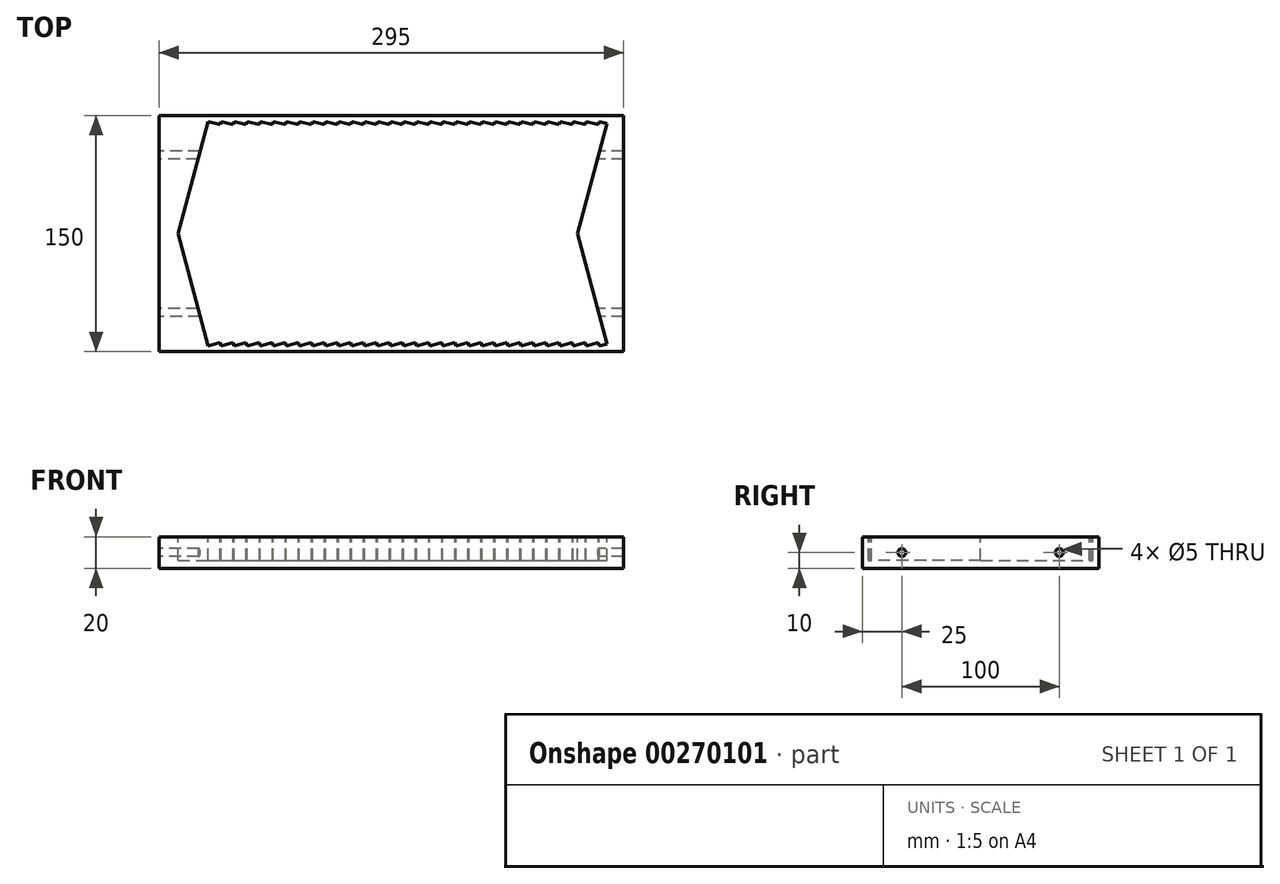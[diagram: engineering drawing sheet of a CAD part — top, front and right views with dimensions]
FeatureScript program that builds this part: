
annotation { "Feature Type Name" : "Feature", "Feature Type Description" : "" }
export const myFeature = defineFeature(function(context is Context, id is Id, definition is map)
    precondition{}
    {
        {
            var Q0;
            Q0=qCreatedBy(makeId("Top.planeOp"),FACE);
            var sketch = newSketch(context, id + "F0", { "sketchPlane" : qUnion([Q0])});
            skLineSegment(sketch, "E0.bottom", {"start": v(147.5, -75) * mm, "end": v(-147.5, -75) * mm});
            skLineSegment(sketch, "E0.top", {"start": v(147.5, 75) * mm, "end": v(-147.5, 75) * mm});
            skLineSegment(sketch, "E0.left", {"start": v(147.5, -75) * mm, "end": v(147.5, 75) * mm});
            skLineSegment(sketch, "E0.right", {"start": v(-147.5, -75) * mm, "end": v(-147.5, 75) * mm});
            skPoint(sketch, "E0.middle", {"position": v(0, 0) * mm});
            skPoint(sketch, "E1", {"position": v(0, 75) * mm});
            skPoint(sketch, "E2", {"position": v(-147.5, 0) * mm});
            skSolve(sketch);
        }
        {
            var Q0;
            Q0=makeQuery(id+"F0.imprint","IMPRINT",FACE,{"disambiguationData":[TD([[makeQuery(id+"F0.imprint","IMPRINT",EDGE,{"derivedFrom":sQuery(id+"F0.wireOp",EDGE,"E0.bottom")}),-1.0]])]});
            extrude(context, id + "F1", {"entities" : qUnion([Q0]), "depth" : 20 * mm});
        }
        {
            var Q0;
            Q0=makeQuery(id+"F1.opExtrude","SWEPT_FACE",FACE,{"disambiguationData":[OSD([sQuery(id+"F0.wireOp",EDGE,"E0.left")])]});
            var sketch = newSketch(context, id + "F2", { "sketchPlane" : qUnion([Q0])});
            skPoint(sketch, "E3", {"position": v(-50, 10) * mm});
            skPoint(sketch, "E4", {"position": v(50, 10) * mm});
            skSolve(sketch);
        }
        {
            var Q0;
            Q0=sQuery(id+"F2.wireOp",VERTEX,"E3");
            var Q1;
            Q1=sQuery(id+"F2.wireOp",VERTEX,"E4");
            var Q2;
            Q2=makeQuery(id+"F1.opExtrude","SWEPT_BODY",BODY,{"disambiguationData":[OSD([sQuery(id+"F0.wireOp",EDGE,"E0.bottom"),sQuery(id+"F0.wireOp",EDGE,"E0.top"),sQuery(id+"F0.wireOp",EDGE,"E0.left"),sQuery(id+"F0.wireOp",EDGE,"E0.right")])]});
            hole(context, id + "F3", {"style" : HoleStyle.SIMPLE, "endStyle" : HoleEndStyle.THROUGH, "standardTappedOrClearance" : lookupTablePath({ "standard" : "ISO", "engagement" : "75%", "pitch" : "1 mm", "size" : "M6", "type" : "Tapped" }), "standardBlindInLast" : lookupTablePath({ "standard" : "ISO", "engagement" : "75%", "pitch" : "1 mm", "size" : "M6", "type" : "Tapped" }), "holeDiameter" : 5 * mm, "showTappedDepth" : true, "tappedDepth" : 40 * mm, "tapClearance" : 3, "startFromSketch" : true, "locations" : qUnion([Q0, Q1]), "scope" : qUnion([Q2]), "majorDiameter" : 6 * mm});
        }
        {
            var Q0;
            Q0=makeQuery(id+"F1.opExtrude","SWEPT_FACE",FACE,{"disambiguationData":[OSD([sQuery(id+"F0.wireOp",EDGE,"E0.right")])]});
            var sketch = newSketch(context, id + "F4", { "sketchPlane" : qUnion([Q0])});
            skPoint(sketch, "E5", {"position": v(0, 10) * mm});
            skLineSegment(sketch, "E6", {"start": v(-50, 10) * mm, "end": v(50, 10) * mm, "construction": true});
            skSolve(sketch);
        }
        {
            var Q0;
            Q0=makeQuery(id+"F1.opExtrude","CAP_FACE",FACE,{"disambiguationData":[OSD([sQuery(id+"F0.wireOp",EDGE,"E0.bottom"),sQuery(id+"F0.wireOp",EDGE,"E0.top"),sQuery(id+"F0.wireOp",EDGE,"E0.left"),sQuery(id+"F0.wireOp",EDGE,"E0.right")])],"isStart":false});
            var sketch = newSketch(context, id + "F5", { "sketchPlane" : qUnion([Q0])});
            skLineSegment(sketch, "E7", {"start": v(-135.5, 0) * mm, "end": v(-116.4, 71.3) * mm});
            skLineSegment(sketch, "E8", {"start": v(-135.5, 0) * mm, "end": v(-116.4, -71.3) * mm});
            skLineSegment(sketch, "E9.0", {"start": v(-130.32, 0) * mm, "end": v(-111.57, 70) * mm});
            skLineSegment(sketch, "E9.1", {"start": v(-130.32, 0) * mm, "end": v(-111.57, -70) * mm});
            skLineSegment(sketch, "E10", {"start": v(-116.4, 71.3) * mm, "end": v(-111.57, 70) * mm});
            skLineSegment(sketch, "E11", {"start": v(-116.4, -71.3) * mm, "end": v(-111.57, -70) * mm});
            skLineSegment(sketch, "E12.0", {"start": v(-127.22, 0) * mm, "end": v(-108.67, 69.22) * mm});
            skLineSegment(sketch, "E12.1", {"start": v(-127.22, 0) * mm, "end": v(-108.67, -69.22) * mm});
            skLineSegment(sketch, "E13", {"start": v(-111.57, 70) * mm, "end": v(-108.67, 69.22) * mm});
            skLineSegment(sketch, "E14", {"start": v(-111.57, -70) * mm, "end": v(-108.67, -69.22) * mm});
            skLineSegment(sketch, "E15.1.0.0", {"start": v(-118.94, 0) * mm, "end": v(-100.39, 69.22) * mm});
            skLineSegment(sketch, "E15.1.0.1", {"start": v(-122.04, 0) * mm, "end": v(-103.28, 70) * mm});
            skLineSegment(sketch, "E15.1.0.2", {"start": v(-127.22, 0) * mm, "end": v(-108.11, 71.3) * mm});
            skLineSegment(sketch, "E15.1.0.3", {"start": v(-127.22, 0) * mm, "end": v(-108.11, -71.3) * mm});
            skLineSegment(sketch, "E15.1.0.4", {"start": v(-122.04, 0) * mm, "end": v(-103.28, -70) * mm});
            skLineSegment(sketch, "E15.1.0.5", {"start": v(-118.94, 0) * mm, "end": v(-100.39, -69.22) * mm});
            skLineSegment(sketch, "E15.1.0.6", {"start": v(-108.11, -71.3) * mm, "end": v(-103.28, -70) * mm});
            skLineSegment(sketch, "E15.1.0.7", {"start": v(-103.28, -70) * mm, "end": v(-100.39, -69.22) * mm});
            skLineSegment(sketch, "E15.1.0.8", {"start": v(-108.11, 71.3) * mm, "end": v(-103.28, 70) * mm});
            skLineSegment(sketch, "E15.1.0.9", {"start": v(-103.28, 70) * mm, "end": v(-100.39, 69.22) * mm});
            skLineSegment(sketch, "E15.2.0.0", {"start": v(-110.65, 0) * mm, "end": v(-92.1, 69.22) * mm});
            skLineSegment(sketch, "E15.2.0.1", {"start": v(-113.76, 0) * mm, "end": v(-95, 70) * mm});
            skLineSegment(sketch, "E15.2.0.2", {"start": v(-118.94, 0) * mm, "end": v(-99.83, 71.3) * mm});
            skLineSegment(sketch, "E15.2.0.3", {"start": v(-118.94, 0) * mm, "end": v(-99.83, -71.3) * mm});
            skLineSegment(sketch, "E15.2.0.4", {"start": v(-113.76, 0) * mm, "end": v(-95, -70) * mm});
            skLineSegment(sketch, "E15.2.0.5", {"start": v(-110.65, 0) * mm, "end": v(-92.1, -69.22) * mm});
            skLineSegment(sketch, "E15.2.0.6", {"start": v(-99.83, -71.3) * mm, "end": v(-95, -70) * mm});
            skLineSegment(sketch, "E15.2.0.7", {"start": v(-95, -70) * mm, "end": v(-92.1, -69.22) * mm});
            skLineSegment(sketch, "E15.2.0.8", {"start": v(-99.83, 71.3) * mm, "end": v(-95, 70) * mm});
            skLineSegment(sketch, "E15.2.0.9", {"start": v(-95, 70) * mm, "end": v(-92.1, 69.22) * mm});
            skLineSegment(sketch, "E15.direction1", {"start": v(-127.22, 0) * mm, "end": v(-118.94, 0) * mm, "construction": true});
            skLineSegment(sketch, "E16.0.3.0", {"start": v(-102.37, 0) * mm, "end": v(-83.82, 69.22) * mm});
            skLineSegment(sketch, "E16.3.3.0", {"start": v(-105.48, 0) * mm, "end": v(-86.72, 70) * mm});
            skLineSegment(sketch, "E16.6.3.0", {"start": v(-110.65, 0) * mm, "end": v(-91.55, 71.3) * mm});
            skLineSegment(sketch, "E16.9.3.0", {"start": v(-110.65, 0) * mm, "end": v(-91.55, -71.3) * mm});
            skLineSegment(sketch, "E16.12.3.0", {"start": v(-105.48, 0) * mm, "end": v(-86.72, -70) * mm});
            skLineSegment(sketch, "E16.15.3.0", {"start": v(-102.37, 0) * mm, "end": v(-83.82, -69.22) * mm});
            skLineSegment(sketch, "E16.18.3.0", {"start": v(-91.55, -71.3) * mm, "end": v(-86.72, -70) * mm});
            skLineSegment(sketch, "E16.21.3.0", {"start": v(-86.72, -70) * mm, "end": v(-83.82, -69.22) * mm});
            skLineSegment(sketch, "E16.24.3.0", {"start": v(-91.55, 71.3) * mm, "end": v(-86.72, 70) * mm});
            skLineSegment(sketch, "E16.27.3.0", {"start": v(-86.72, 70) * mm, "end": v(-83.82, 69.22) * mm});
            skLineSegment(sketch, "E16.0.4.0", {"start": v(-94.09, 0) * mm, "end": v(-75.54, 69.22) * mm});
            skLineSegment(sketch, "E16.3.4.0", {"start": v(-97.2, 0) * mm, "end": v(-78.44, 70) * mm});
            skLineSegment(sketch, "E16.6.4.0", {"start": v(-102.37, 0) * mm, "end": v(-83.27, 71.3) * mm});
            skLineSegment(sketch, "E16.9.4.0", {"start": v(-102.37, 0) * mm, "end": v(-83.27, -71.3) * mm});
            skLineSegment(sketch, "E16.12.4.0", {"start": v(-97.2, 0) * mm, "end": v(-78.44, -70) * mm});
            skLineSegment(sketch, "E16.15.4.0", {"start": v(-94.09, 0) * mm, "end": v(-75.54, -69.22) * mm});
            skLineSegment(sketch, "E16.18.4.0", {"start": v(-83.27, -71.3) * mm, "end": v(-78.44, -70) * mm});
            skLineSegment(sketch, "E16.21.4.0", {"start": v(-78.44, -70) * mm, "end": v(-75.54, -69.22) * mm});
            skLineSegment(sketch, "E16.24.4.0", {"start": v(-83.27, 71.3) * mm, "end": v(-78.44, 70) * mm});
            skLineSegment(sketch, "E16.27.4.0", {"start": v(-78.44, 70) * mm, "end": v(-75.54, 69.22) * mm});
            skLineSegment(sketch, "E16.0.5.0", {"start": v(-85.8, 0) * mm, "end": v(-67.26, 69.22) * mm});
            skLineSegment(sketch, "E16.3.5.0", {"start": v(-88.91, 0) * mm, "end": v(-70.16, 70) * mm});
            skLineSegment(sketch, "E16.6.5.0", {"start": v(-94.09, 0) * mm, "end": v(-74.99, 71.3) * mm});
            skLineSegment(sketch, "E16.9.5.0", {"start": v(-94.09, 0) * mm, "end": v(-74.99, -71.3) * mm});
            skLineSegment(sketch, "E16.12.5.0", {"start": v(-88.91, 0) * mm, "end": v(-70.16, -70) * mm});
            skLineSegment(sketch, "E16.15.5.0", {"start": v(-85.8, 0) * mm, "end": v(-67.26, -69.22) * mm});
            skLineSegment(sketch, "E16.18.5.0", {"start": v(-74.99, -71.3) * mm, "end": v(-70.16, -70) * mm});
            skLineSegment(sketch, "E16.21.5.0", {"start": v(-70.16, -70) * mm, "end": v(-67.26, -69.22) * mm});
            skLineSegment(sketch, "E16.24.5.0", {"start": v(-74.99, 71.3) * mm, "end": v(-70.16, 70) * mm});
            skLineSegment(sketch, "E16.27.5.0", {"start": v(-70.16, 70) * mm, "end": v(-67.26, 69.22) * mm});
            skLineSegment(sketch, "E16.0.6.0", {"start": v(-77.52, 0) * mm, "end": v(-58.98, 69.22) * mm});
            skLineSegment(sketch, "E16.3.6.0", {"start": v(-80.63, 0) * mm, "end": v(-61.87, 70) * mm});
            skLineSegment(sketch, "E16.6.6.0", {"start": v(-85.8, 0) * mm, "end": v(-66.7, 71.3) * mm});
            skLineSegment(sketch, "E16.9.6.0", {"start": v(-85.8, 0) * mm, "end": v(-66.7, -71.3) * mm});
            skLineSegment(sketch, "E16.12.6.0", {"start": v(-80.63, 0) * mm, "end": v(-61.87, -70) * mm});
            skLineSegment(sketch, "E16.15.6.0", {"start": v(-77.52, 0) * mm, "end": v(-58.98, -69.22) * mm});
            skLineSegment(sketch, "E16.18.6.0", {"start": v(-66.7, -71.3) * mm, "end": v(-61.87, -70) * mm});
            skLineSegment(sketch, "E16.21.6.0", {"start": v(-61.87, -70) * mm, "end": v(-58.98, -69.22) * mm});
            skLineSegment(sketch, "E16.24.6.0", {"start": v(-66.7, 71.3) * mm, "end": v(-61.87, 70) * mm});
            skLineSegment(sketch, "E16.27.6.0", {"start": v(-61.87, 70) * mm, "end": v(-58.98, 69.22) * mm});
            skLineSegment(sketch, "E16.0.7.0", {"start": v(-69.24, 0) * mm, "end": v(-50.7, 69.22) * mm});
            skLineSegment(sketch, "E16.3.7.0", {"start": v(-72.35, 0) * mm, "end": v(-53.6, 70) * mm});
            skLineSegment(sketch, "E16.6.7.0", {"start": v(-77.52, 0) * mm, "end": v(-58.42, 71.3) * mm});
            skLineSegment(sketch, "E16.9.7.0", {"start": v(-77.52, 0) * mm, "end": v(-58.42, -71.3) * mm});
            skLineSegment(sketch, "E16.12.7.0", {"start": v(-72.35, 0) * mm, "end": v(-53.6, -70) * mm});
            skLineSegment(sketch, "E16.15.7.0", {"start": v(-69.24, 0) * mm, "end": v(-50.7, -69.22) * mm});
            skLineSegment(sketch, "E16.18.7.0", {"start": v(-58.42, -71.3) * mm, "end": v(-53.6, -70) * mm});
            skLineSegment(sketch, "E16.21.7.0", {"start": v(-53.6, -70) * mm, "end": v(-50.7, -69.22) * mm});
            skLineSegment(sketch, "E16.24.7.0", {"start": v(-58.42, 71.3) * mm, "end": v(-53.6, 70) * mm});
            skLineSegment(sketch, "E16.27.7.0", {"start": v(-53.6, 70) * mm, "end": v(-50.7, 69.22) * mm});
            skLineSegment(sketch, "E16.0.8.0", {"start": v(-60.96, 0) * mm, "end": v(-42.41, 69.22) * mm});
            skLineSegment(sketch, "E16.3.8.0", {"start": v(-64.07, 0) * mm, "end": v(-45.3, 70) * mm});
            skLineSegment(sketch, "E16.6.8.0", {"start": v(-69.24, 0) * mm, "end": v(-50.14, 71.3) * mm});
            skLineSegment(sketch, "E16.9.8.0", {"start": v(-69.24, 0) * mm, "end": v(-50.14, -71.3) * mm});
            skLineSegment(sketch, "E16.12.8.0", {"start": v(-64.07, 0) * mm, "end": v(-45.3, -70) * mm});
            skLineSegment(sketch, "E16.15.8.0", {"start": v(-60.96, 0) * mm, "end": v(-42.41, -69.22) * mm});
            skLineSegment(sketch, "E16.18.8.0", {"start": v(-50.14, -71.3) * mm, "end": v(-45.3, -70) * mm});
            skLineSegment(sketch, "E16.21.8.0", {"start": v(-45.3, -70) * mm, "end": v(-42.41, -69.22) * mm});
            skLineSegment(sketch, "E16.24.8.0", {"start": v(-50.14, 71.3) * mm, "end": v(-45.3, 70) * mm});
            skLineSegment(sketch, "E16.27.8.0", {"start": v(-45.3, 70) * mm, "end": v(-42.41, 69.22) * mm});
            skLineSegment(sketch, "E16.0.9.0", {"start": v(-52.68, 0) * mm, "end": v(-34.13, 69.22) * mm});
            skLineSegment(sketch, "E16.3.9.0", {"start": v(-55.78, 0) * mm, "end": v(-37.03, 70) * mm});
            skLineSegment(sketch, "E16.6.9.0", {"start": v(-60.96, 0) * mm, "end": v(-41.86, 71.3) * mm});
            skLineSegment(sketch, "E16.9.9.0", {"start": v(-60.96, 0) * mm, "end": v(-41.86, -71.3) * mm});
            skLineSegment(sketch, "E16.12.9.0", {"start": v(-55.78, 0) * mm, "end": v(-37.03, -70) * mm});
            skLineSegment(sketch, "E16.15.9.0", {"start": v(-52.68, 0) * mm, "end": v(-34.13, -69.22) * mm});
            skLineSegment(sketch, "E16.18.9.0", {"start": v(-41.86, -71.3) * mm, "end": v(-37.03, -70) * mm});
            skLineSegment(sketch, "E16.21.9.0", {"start": v(-37.03, -70) * mm, "end": v(-34.13, -69.22) * mm});
            skLineSegment(sketch, "E16.24.9.0", {"start": v(-41.86, 71.3) * mm, "end": v(-37.03, 70) * mm});
            skLineSegment(sketch, "E16.27.9.0", {"start": v(-37.03, 70) * mm, "end": v(-34.13, 69.22) * mm});
            skLineSegment(sketch, "E16.0.10.0", {"start": v(-44.4, 0) * mm, "end": v(-25.85, 69.22) * mm});
            skLineSegment(sketch, "E16.3.10.0", {"start": v(-47.5, 0) * mm, "end": v(-28.75, 70) * mm});
            skLineSegment(sketch, "E16.6.10.0", {"start": v(-52.68, 0) * mm, "end": v(-33.57, 71.3) * mm});
            skLineSegment(sketch, "E16.9.10.0", {"start": v(-52.68, 0) * mm, "end": v(-33.57, -71.3) * mm});
            skLineSegment(sketch, "E16.12.10.0", {"start": v(-47.5, 0) * mm, "end": v(-28.75, -70) * mm});
            skLineSegment(sketch, "E16.15.10.0", {"start": v(-44.4, 0) * mm, "end": v(-25.85, -69.22) * mm});
            skLineSegment(sketch, "E16.18.10.0", {"start": v(-33.57, -71.3) * mm, "end": v(-28.75, -70) * mm});
            skLineSegment(sketch, "E16.21.10.0", {"start": v(-28.75, -70) * mm, "end": v(-25.85, -69.22) * mm});
            skLineSegment(sketch, "E16.24.10.0", {"start": v(-33.57, 71.3) * mm, "end": v(-28.75, 70) * mm});
            skLineSegment(sketch, "E16.27.10.0", {"start": v(-28.75, 70) * mm, "end": v(-25.85, 69.22) * mm});
            skLineSegment(sketch, "E16.0.11.0", {"start": v(-36.11, 0) * mm, "end": v(-17.57, 69.22) * mm});
            skLineSegment(sketch, "E16.3.11.0", {"start": v(-39.22, 0) * mm, "end": v(-20.46, 70) * mm});
            skLineSegment(sketch, "E16.6.11.0", {"start": v(-44.4, 0) * mm, "end": v(-25.3, 71.3) * mm});
            skLineSegment(sketch, "E16.9.11.0", {"start": v(-44.4, 0) * mm, "end": v(-25.3, -71.3) * mm});
            skLineSegment(sketch, "E16.12.11.0", {"start": v(-39.22, 0) * mm, "end": v(-20.46, -70) * mm});
            skLineSegment(sketch, "E16.15.11.0", {"start": v(-36.11, 0) * mm, "end": v(-17.57, -69.22) * mm});
            skLineSegment(sketch, "E16.18.11.0", {"start": v(-25.3, -71.3) * mm, "end": v(-20.46, -70) * mm});
            skLineSegment(sketch, "E16.21.11.0", {"start": v(-20.46, -70) * mm, "end": v(-17.57, -69.22) * mm});
            skLineSegment(sketch, "E16.24.11.0", {"start": v(-25.3, 71.3) * mm, "end": v(-20.46, 70) * mm});
            skLineSegment(sketch, "E16.27.11.0", {"start": v(-20.46, 70) * mm, "end": v(-17.57, 69.22) * mm});
            skLineSegment(sketch, "E16.0.12.0", {"start": v(-27.83, 0) * mm, "end": v(-9.28, 69.22) * mm});
            skLineSegment(sketch, "E16.3.12.0", {"start": v(-30.94, 0) * mm, "end": v(-12.18, 70) * mm});
            skLineSegment(sketch, "E16.6.12.0", {"start": v(-36.11, 0) * mm, "end": v(-17.01, 71.3) * mm});
            skLineSegment(sketch, "E16.9.12.0", {"start": v(-36.11, 0) * mm, "end": v(-17.01, -71.3) * mm});
            skLineSegment(sketch, "E16.12.12.0", {"start": v(-30.94, 0) * mm, "end": v(-12.18, -70) * mm});
            skLineSegment(sketch, "E16.15.12.0", {"start": v(-27.83, 0) * mm, "end": v(-9.28, -69.22) * mm});
            skLineSegment(sketch, "E16.18.12.0", {"start": v(-17.01, -71.3) * mm, "end": v(-12.18, -70) * mm});
            skLineSegment(sketch, "E16.21.12.0", {"start": v(-12.18, -70) * mm, "end": v(-9.28, -69.22) * mm});
            skLineSegment(sketch, "E16.24.12.0", {"start": v(-17.01, 71.3) * mm, "end": v(-12.18, 70) * mm});
            skLineSegment(sketch, "E16.27.12.0", {"start": v(-12.18, 70) * mm, "end": v(-9.28, 69.22) * mm});
            skLineSegment(sketch, "E16.0.13.0", {"start": v(-19.55, 0) * mm, "end": v(-1, 69.22) * mm});
            skLineSegment(sketch, "E16.3.13.0", {"start": v(-22.65, 0) * mm, "end": v(-3.9, 70) * mm});
            skLineSegment(sketch, "E16.6.13.0", {"start": v(-27.83, 0) * mm, "end": v(-8.73, 71.3) * mm});
            skLineSegment(sketch, "E16.9.13.0", {"start": v(-27.83, 0) * mm, "end": v(-8.73, -71.3) * mm});
            skLineSegment(sketch, "E16.12.13.0", {"start": v(-22.65, 0) * mm, "end": v(-3.9, -70) * mm});
            skLineSegment(sketch, "E16.15.13.0", {"start": v(-19.55, 0) * mm, "end": v(-1, -69.22) * mm});
            skLineSegment(sketch, "E16.18.13.0", {"start": v(-8.73, -71.3) * mm, "end": v(-3.9, -70) * mm});
            skLineSegment(sketch, "E16.21.13.0", {"start": v(-3.9, -70) * mm, "end": v(-1, -69.22) * mm});
            skLineSegment(sketch, "E16.24.13.0", {"start": v(-8.73, 71.3) * mm, "end": v(-3.9, 70) * mm});
            skLineSegment(sketch, "E16.27.13.0", {"start": v(-3.9, 70) * mm, "end": v(-1, 69.22) * mm});
            skLineSegment(sketch, "E16.0.14.0", {"start": v(-11.27, 0) * mm, "end": v(7.28, 69.22) * mm});
            skLineSegment(sketch, "E16.3.14.0", {"start": v(-14.37, 0) * mm, "end": v(4.38, 70) * mm});
            skLineSegment(sketch, "E16.6.14.0", {"start": v(-19.55, 0) * mm, "end": v(-0.45, 71.3) * mm});
            skLineSegment(sketch, "E16.9.14.0", {"start": v(-19.55, 0) * mm, "end": v(-0.45, -71.3) * mm});
            skLineSegment(sketch, "E16.12.14.0", {"start": v(-14.37, 0) * mm, "end": v(4.38, -70) * mm});
            skLineSegment(sketch, "E16.15.14.0", {"start": v(-11.27, 0) * mm, "end": v(7.28, -69.22) * mm});
            skLineSegment(sketch, "E16.18.14.0", {"start": v(-0.45, -71.3) * mm, "end": v(4.38, -70) * mm});
            skLineSegment(sketch, "E16.21.14.0", {"start": v(4.38, -70) * mm, "end": v(7.28, -69.22) * mm});
            skLineSegment(sketch, "E16.24.14.0", {"start": v(-0.45, 71.3) * mm, "end": v(4.38, 70) * mm});
            skLineSegment(sketch, "E16.27.14.0", {"start": v(4.38, 70) * mm, "end": v(7.28, 69.22) * mm});
            skLineSegment(sketch, "E16.0.15.0", {"start": v(-2.98, 0) * mm, "end": v(15.56, 69.22) * mm});
            skLineSegment(sketch, "E16.3.15.0", {"start": v(-6.1, 0) * mm, "end": v(12.67, 70) * mm});
            skLineSegment(sketch, "E16.6.15.0", {"start": v(-11.27, 0) * mm, "end": v(7.84, 71.3) * mm});
            skLineSegment(sketch, "E16.9.15.0", {"start": v(-11.27, 0) * mm, "end": v(7.84, -71.3) * mm});
            skLineSegment(sketch, "E16.12.15.0", {"start": v(-6.1, 0) * mm, "end": v(12.67, -70) * mm});
            skLineSegment(sketch, "E16.15.15.0", {"start": v(-2.98, 0) * mm, "end": v(15.56, -69.22) * mm});
            skLineSegment(sketch, "E16.18.15.0", {"start": v(7.84, -71.3) * mm, "end": v(12.67, -70) * mm});
            skLineSegment(sketch, "E16.21.15.0", {"start": v(12.67, -70) * mm, "end": v(15.56, -69.22) * mm});
            skLineSegment(sketch, "E16.24.15.0", {"start": v(7.84, 71.3) * mm, "end": v(12.67, 70) * mm});
            skLineSegment(sketch, "E16.27.15.0", {"start": v(12.67, 70) * mm, "end": v(15.56, 69.22) * mm});
            skLineSegment(sketch, "E16.0.16.0", {"start": v(5.3, 0) * mm, "end": v(23.85, 69.22) * mm});
            skLineSegment(sketch, "E16.3.16.0", {"start": v(2.2, 0) * mm, "end": v(20.95, 70) * mm});
            skLineSegment(sketch, "E16.6.16.0", {"start": v(-2.98, 0) * mm, "end": v(16.12, 71.3) * mm});
            skLineSegment(sketch, "E16.9.16.0", {"start": v(-2.98, 0) * mm, "end": v(16.12, -71.3) * mm});
            skLineSegment(sketch, "E16.12.16.0", {"start": v(2.2, 0) * mm, "end": v(20.95, -70) * mm});
            skLineSegment(sketch, "E16.15.16.0", {"start": v(5.3, 0) * mm, "end": v(23.85, -69.22) * mm});
            skLineSegment(sketch, "E16.18.16.0", {"start": v(16.12, -71.3) * mm, "end": v(20.95, -70) * mm});
            skLineSegment(sketch, "E16.21.16.0", {"start": v(20.95, -70) * mm, "end": v(23.85, -69.22) * mm});
            skLineSegment(sketch, "E16.24.16.0", {"start": v(16.12, 71.3) * mm, "end": v(20.95, 70) * mm});
            skLineSegment(sketch, "E16.27.16.0", {"start": v(20.95, 70) * mm, "end": v(23.85, 69.22) * mm});
            skLineSegment(sketch, "E16.0.17.0", {"start": v(13.58, 0) * mm, "end": v(32.13, 69.22) * mm});
            skLineSegment(sketch, "E16.3.17.0", {"start": v(10.47, 0) * mm, "end": v(29.23, 70) * mm});
            skLineSegment(sketch, "E16.6.17.0", {"start": v(5.3, 0) * mm, "end": v(24.4, 71.3) * mm});
            skLineSegment(sketch, "E16.9.17.0", {"start": v(5.3, 0) * mm, "end": v(24.4, -71.3) * mm});
            skLineSegment(sketch, "E16.12.17.0", {"start": v(10.47, 0) * mm, "end": v(29.23, -70) * mm});
            skLineSegment(sketch, "E16.15.17.0", {"start": v(13.58, 0) * mm, "end": v(32.13, -69.22) * mm});
            skLineSegment(sketch, "E16.18.17.0", {"start": v(24.4, -71.3) * mm, "end": v(29.23, -70) * mm});
            skLineSegment(sketch, "E16.21.17.0", {"start": v(29.23, -70) * mm, "end": v(32.13, -69.22) * mm});
            skLineSegment(sketch, "E16.24.17.0", {"start": v(24.4, 71.3) * mm, "end": v(29.23, 70) * mm});
            skLineSegment(sketch, "E16.27.17.0", {"start": v(29.23, 70) * mm, "end": v(32.13, 69.22) * mm});
            skLineSegment(sketch, "E16.0.18.0", {"start": v(21.86, 0) * mm, "end": v(40.41, 69.22) * mm});
            skLineSegment(sketch, "E16.3.18.0", {"start": v(18.76, 0) * mm, "end": v(37.51, 70) * mm});
            skLineSegment(sketch, "E16.6.18.0", {"start": v(13.58, 0) * mm, "end": v(32.68, 71.3) * mm});
            skLineSegment(sketch, "E16.9.18.0", {"start": v(13.58, 0) * mm, "end": v(32.68, -71.3) * mm});
            skLineSegment(sketch, "E16.12.18.0", {"start": v(18.76, 0) * mm, "end": v(37.51, -70) * mm});
            skLineSegment(sketch, "E16.15.18.0", {"start": v(21.86, 0) * mm, "end": v(40.41, -69.22) * mm});
            skLineSegment(sketch, "E16.18.18.0", {"start": v(32.68, -71.3) * mm, "end": v(37.51, -70) * mm});
            skLineSegment(sketch, "E16.21.18.0", {"start": v(37.51, -70) * mm, "end": v(40.41, -69.22) * mm});
            skLineSegment(sketch, "E16.24.18.0", {"start": v(32.68, 71.3) * mm, "end": v(37.51, 70) * mm});
            skLineSegment(sketch, "E16.27.18.0", {"start": v(37.51, 70) * mm, "end": v(40.41, 69.22) * mm});
            skLineSegment(sketch, "E16.0.19.0", {"start": v(30.14, 0) * mm, "end": v(48.7, 69.22) * mm});
            skLineSegment(sketch, "E16.3.19.0", {"start": v(27.04, 0) * mm, "end": v(45.8, 70) * mm});
            skLineSegment(sketch, "E16.6.19.0", {"start": v(21.86, 0) * mm, "end": v(40.97, 71.3) * mm});
            skLineSegment(sketch, "E16.9.19.0", {"start": v(21.86, 0) * mm, "end": v(40.97, -71.3) * mm});
            skLineSegment(sketch, "E16.12.19.0", {"start": v(27.04, 0) * mm, "end": v(45.8, -70) * mm});
            skLineSegment(sketch, "E16.15.19.0", {"start": v(30.14, 0) * mm, "end": v(48.7, -69.22) * mm});
            skLineSegment(sketch, "E16.18.19.0", {"start": v(40.97, -71.3) * mm, "end": v(45.8, -70) * mm});
            skLineSegment(sketch, "E16.21.19.0", {"start": v(45.8, -70) * mm, "end": v(48.7, -69.22) * mm});
            skLineSegment(sketch, "E16.24.19.0", {"start": v(40.97, 71.3) * mm, "end": v(45.8, 70) * mm});
            skLineSegment(sketch, "E16.27.19.0", {"start": v(45.8, 70) * mm, "end": v(48.7, 69.22) * mm});
            skLineSegment(sketch, "E16.0.20.0", {"start": v(38.43, 0) * mm, "end": v(56.97, 69.22) * mm});
            skLineSegment(sketch, "E16.3.20.0", {"start": v(35.32, 0) * mm, "end": v(54.08, 70) * mm});
            skLineSegment(sketch, "E16.6.20.0", {"start": v(30.14, 0) * mm, "end": v(49.25, 71.3) * mm});
            skLineSegment(sketch, "E16.9.20.0", {"start": v(30.14, 0) * mm, "end": v(49.25, -71.3) * mm});
            skLineSegment(sketch, "E16.12.20.0", {"start": v(35.32, 0) * mm, "end": v(54.08, -70) * mm});
            skLineSegment(sketch, "E16.15.20.0", {"start": v(38.43, 0) * mm, "end": v(56.97, -69.22) * mm});
            skLineSegment(sketch, "E16.18.20.0", {"start": v(49.25, -71.3) * mm, "end": v(54.08, -70) * mm});
            skLineSegment(sketch, "E16.21.20.0", {"start": v(54.08, -70) * mm, "end": v(56.97, -69.22) * mm});
            skLineSegment(sketch, "E16.24.20.0", {"start": v(49.25, 71.3) * mm, "end": v(54.08, 70) * mm});
            skLineSegment(sketch, "E16.27.20.0", {"start": v(54.08, 70) * mm, "end": v(56.97, 69.22) * mm});
            skLineSegment(sketch, "E16.0.21.0", {"start": v(46.7, 0) * mm, "end": v(65.26, 69.22) * mm});
            skLineSegment(sketch, "E16.3.21.0", {"start": v(43.6, 0) * mm, "end": v(62.36, 70) * mm});
            skLineSegment(sketch, "E16.6.21.0", {"start": v(38.43, 0) * mm, "end": v(57.53, 71.3) * mm});
            skLineSegment(sketch, "E16.9.21.0", {"start": v(38.43, 0) * mm, "end": v(57.53, -71.3) * mm});
            skLineSegment(sketch, "E16.12.21.0", {"start": v(43.6, 0) * mm, "end": v(62.36, -70) * mm});
            skLineSegment(sketch, "E16.15.21.0", {"start": v(46.7, 0) * mm, "end": v(65.26, -69.22) * mm});
            skLineSegment(sketch, "E16.18.21.0", {"start": v(57.53, -71.3) * mm, "end": v(62.36, -70) * mm});
            skLineSegment(sketch, "E16.21.21.0", {"start": v(62.36, -70) * mm, "end": v(65.26, -69.22) * mm});
            skLineSegment(sketch, "E16.24.21.0", {"start": v(57.53, 71.3) * mm, "end": v(62.36, 70) * mm});
            skLineSegment(sketch, "E16.27.21.0", {"start": v(62.36, 70) * mm, "end": v(65.26, 69.22) * mm});
            skLineSegment(sketch, "E16.0.22.0", {"start": v(55, 0) * mm, "end": v(73.54, 69.22) * mm});
            skLineSegment(sketch, "E16.3.22.0", {"start": v(51.89, 0) * mm, "end": v(70.64, 70) * mm});
            skLineSegment(sketch, "E16.6.22.0", {"start": v(46.7, 0) * mm, "end": v(65.81, 71.3) * mm});
            skLineSegment(sketch, "E16.9.22.0", {"start": v(46.7, 0) * mm, "end": v(65.81, -71.3) * mm});
            skLineSegment(sketch, "E16.12.22.0", {"start": v(51.89, 0) * mm, "end": v(70.64, -70) * mm});
            skLineSegment(sketch, "E16.15.22.0", {"start": v(55, 0) * mm, "end": v(73.54, -69.22) * mm});
            skLineSegment(sketch, "E16.18.22.0", {"start": v(65.81, -71.3) * mm, "end": v(70.64, -70) * mm});
            skLineSegment(sketch, "E16.21.22.0", {"start": v(70.64, -70) * mm, "end": v(73.54, -69.22) * mm});
            skLineSegment(sketch, "E16.24.22.0", {"start": v(65.81, 71.3) * mm, "end": v(70.64, 70) * mm});
            skLineSegment(sketch, "E16.27.22.0", {"start": v(70.64, 70) * mm, "end": v(73.54, 69.22) * mm});
            skLineSegment(sketch, "E17.0.23.0", {"start": v(63.27, 0) * mm, "end": v(81.82, 69.22) * mm});
            skLineSegment(sketch, "E17.3.23.0", {"start": v(60.17, 0) * mm, "end": v(78.92, 70) * mm});
            skLineSegment(sketch, "E17.6.23.0", {"start": v(55, 0) * mm, "end": v(74.1, 71.3) * mm});
            skLineSegment(sketch, "E17.9.23.0", {"start": v(55, 0) * mm, "end": v(74.1, -71.3) * mm});
            skLineSegment(sketch, "E17.12.23.0", {"start": v(60.17, 0) * mm, "end": v(78.92, -70) * mm});
            skLineSegment(sketch, "E17.15.23.0", {"start": v(63.27, 0) * mm, "end": v(81.82, -69.22) * mm});
            skLineSegment(sketch, "E17.18.23.0", {"start": v(74.1, -71.3) * mm, "end": v(78.92, -70) * mm});
            skLineSegment(sketch, "E17.21.23.0", {"start": v(78.92, -70) * mm, "end": v(81.82, -69.22) * mm});
            skLineSegment(sketch, "E17.24.23.0", {"start": v(74.1, 71.3) * mm, "end": v(78.92, 70) * mm});
            skLineSegment(sketch, "E17.27.23.0", {"start": v(78.92, 70) * mm, "end": v(81.82, 69.22) * mm});
            skLineSegment(sketch, "E17.0.24.0", {"start": v(71.56, 0) * mm, "end": v(90.1, 69.22) * mm});
            skLineSegment(sketch, "E17.3.24.0", {"start": v(68.45, 0) * mm, "end": v(87.2, 70) * mm});
            skLineSegment(sketch, "E17.6.24.0", {"start": v(63.27, 0) * mm, "end": v(82.38, 71.3) * mm});
            skLineSegment(sketch, "E17.9.24.0", {"start": v(63.27, 0) * mm, "end": v(82.38, -71.3) * mm});
            skLineSegment(sketch, "E17.12.24.0", {"start": v(68.45, 0) * mm, "end": v(87.2, -70) * mm});
            skLineSegment(sketch, "E17.15.24.0", {"start": v(71.56, 0) * mm, "end": v(90.1, -69.22) * mm});
            skLineSegment(sketch, "E17.18.24.0", {"start": v(82.38, -71.3) * mm, "end": v(87.2, -70) * mm});
            skLineSegment(sketch, "E17.21.24.0", {"start": v(87.2, -70) * mm, "end": v(90.1, -69.22) * mm});
            skLineSegment(sketch, "E17.24.24.0", {"start": v(82.38, 71.3) * mm, "end": v(87.2, 70) * mm});
            skLineSegment(sketch, "E17.27.24.0", {"start": v(87.2, 70) * mm, "end": v(90.1, 69.22) * mm});
            skLineSegment(sketch, "E18.0.25.0", {"start": v(79.84, 0) * mm, "end": v(98.39, 69.22) * mm});
            skLineSegment(sketch, "E18.3.25.0", {"start": v(76.73, 0) * mm, "end": v(95.49, 70) * mm});
            skLineSegment(sketch, "E18.6.25.0", {"start": v(71.56, 0) * mm, "end": v(90.66, 71.3) * mm});
            skLineSegment(sketch, "E18.9.25.0", {"start": v(71.56, 0) * mm, "end": v(90.66, -71.3) * mm});
            skLineSegment(sketch, "E18.12.25.0", {"start": v(76.73, 0) * mm, "end": v(95.49, -70) * mm});
            skLineSegment(sketch, "E18.15.25.0", {"start": v(79.84, 0) * mm, "end": v(98.39, -69.22) * mm});
            skLineSegment(sketch, "E18.18.25.0", {"start": v(90.66, -71.3) * mm, "end": v(95.49, -70) * mm});
            skLineSegment(sketch, "E18.21.25.0", {"start": v(95.49, -70) * mm, "end": v(98.39, -69.22) * mm});
            skLineSegment(sketch, "E18.24.25.0", {"start": v(90.66, 71.3) * mm, "end": v(95.49, 70) * mm});
            skLineSegment(sketch, "E18.27.25.0", {"start": v(95.49, 70) * mm, "end": v(98.39, 69.22) * mm});
            skLineSegment(sketch, "E18.0.26.0", {"start": v(88.12, 0) * mm, "end": v(106.67, 69.22) * mm});
            skLineSegment(sketch, "E18.3.26.0", {"start": v(85.01, 0) * mm, "end": v(103.77, 70) * mm});
            skLineSegment(sketch, "E18.6.26.0", {"start": v(79.84, 0) * mm, "end": v(98.94, 71.3) * mm});
            skLineSegment(sketch, "E18.9.26.0", {"start": v(79.84, 0) * mm, "end": v(98.94, -71.3) * mm});
            skLineSegment(sketch, "E18.12.26.0", {"start": v(85.01, 0) * mm, "end": v(103.77, -70) * mm});
            skLineSegment(sketch, "E18.15.26.0", {"start": v(88.12, 0) * mm, "end": v(106.67, -69.22) * mm});
            skLineSegment(sketch, "E18.18.26.0", {"start": v(98.94, -71.3) * mm, "end": v(103.77, -70) * mm});
            skLineSegment(sketch, "E18.21.26.0", {"start": v(103.77, -70) * mm, "end": v(106.67, -69.22) * mm});
            skLineSegment(sketch, "E18.24.26.0", {"start": v(98.94, 71.3) * mm, "end": v(103.77, 70) * mm});
            skLineSegment(sketch, "E18.27.26.0", {"start": v(103.77, 70) * mm, "end": v(106.67, 69.22) * mm});
            skLineSegment(sketch, "E18.0.27.0", {"start": v(96.4, 0) * mm, "end": v(114.95, 69.22) * mm});
            skLineSegment(sketch, "E18.3.27.0", {"start": v(93.3, 0) * mm, "end": v(112.05, 70) * mm});
            skLineSegment(sketch, "E18.6.27.0", {"start": v(88.12, 0) * mm, "end": v(107.22, 71.3) * mm});
            skLineSegment(sketch, "E18.9.27.0", {"start": v(88.12, 0) * mm, "end": v(107.22, -71.3) * mm});
            skLineSegment(sketch, "E18.12.27.0", {"start": v(93.3, 0) * mm, "end": v(112.05, -70) * mm});
            skLineSegment(sketch, "E18.15.27.0", {"start": v(96.4, 0) * mm, "end": v(114.95, -69.22) * mm});
            skLineSegment(sketch, "E18.18.27.0", {"start": v(107.22, -71.3) * mm, "end": v(112.05, -70) * mm});
            skLineSegment(sketch, "E18.21.27.0", {"start": v(112.05, -70) * mm, "end": v(114.95, -69.22) * mm});
            skLineSegment(sketch, "E18.24.27.0", {"start": v(107.22, 71.3) * mm, "end": v(112.05, 70) * mm});
            skLineSegment(sketch, "E18.27.27.0", {"start": v(112.05, 70) * mm, "end": v(114.95, 69.22) * mm});
            skLineSegment(sketch, "E19.0.28.0", {"start": v(104.68, 0) * mm, "end": v(123.23, 69.22) * mm});
            skLineSegment(sketch, "E19.3.28.0", {"start": v(101.58, 0) * mm, "end": v(120.33, 70) * mm});
            skLineSegment(sketch, "E19.6.28.0", {"start": v(96.4, 0) * mm, "end": v(115.5, 71.3) * mm});
            skLineSegment(sketch, "E19.9.28.0", {"start": v(96.4, 0) * mm, "end": v(115.5, -71.3) * mm});
            skLineSegment(sketch, "E19.12.28.0", {"start": v(101.58, 0) * mm, "end": v(120.33, -70) * mm});
            skLineSegment(sketch, "E19.15.28.0", {"start": v(104.68, 0) * mm, "end": v(123.23, -69.22) * mm});
            skLineSegment(sketch, "E19.18.28.0", {"start": v(115.5, -71.3) * mm, "end": v(120.33, -70) * mm});
            skLineSegment(sketch, "E19.21.28.0", {"start": v(120.33, -70) * mm, "end": v(123.23, -69.22) * mm});
            skLineSegment(sketch, "E19.24.28.0", {"start": v(115.5, 71.3) * mm, "end": v(120.33, 70) * mm});
            skLineSegment(sketch, "E19.27.28.0", {"start": v(120.33, 70) * mm, "end": v(123.23, 69.22) * mm});
            skLineSegment(sketch, "E19.0.29.0", {"start": v(112.97, 0) * mm, "end": v(131.51, 69.22) * mm});
            skLineSegment(sketch, "E19.3.29.0", {"start": v(109.86, 0) * mm, "end": v(128.62, 70) * mm});
            skLineSegment(sketch, "E19.6.29.0", {"start": v(104.68, 0) * mm, "end": v(123.79, 71.3) * mm});
            skLineSegment(sketch, "E19.9.29.0", {"start": v(104.68, 0) * mm, "end": v(123.79, -71.3) * mm});
            skLineSegment(sketch, "E19.12.29.0", {"start": v(109.86, 0) * mm, "end": v(128.62, -70) * mm});
            skLineSegment(sketch, "E19.15.29.0", {"start": v(112.97, 0) * mm, "end": v(131.51, -69.22) * mm});
            skLineSegment(sketch, "E19.18.29.0", {"start": v(123.79, -71.3) * mm, "end": v(128.62, -70) * mm});
            skLineSegment(sketch, "E19.21.29.0", {"start": v(128.62, -70) * mm, "end": v(131.51, -69.22) * mm});
            skLineSegment(sketch, "E19.24.29.0", {"start": v(123.79, 71.3) * mm, "end": v(128.62, 70) * mm});
            skLineSegment(sketch, "E19.27.29.0", {"start": v(128.62, 70) * mm, "end": v(131.51, 69.22) * mm});
            skLineSegment(sketch, "E20", {"start": v(112.97, 0) * mm, "end": v(132.07, 71.3) * mm});
            skLineSegment(sketch, "E21", {"start": v(112.97, 0) * mm, "end": v(132.07, -71.3) * mm});
            skLineSegment(sketch, "E22.0", {"start": v(118.14, 0) * mm, "end": v(136.9, 70) * mm});
            skLineSegment(sketch, "E22.1", {"start": v(118.14, 0) * mm, "end": v(136.9, -70) * mm});
            skLineSegment(sketch, "E23", {"start": v(132.07, 71.3) * mm, "end": v(136.9, 70) * mm});
            skLineSegment(sketch, "E24", {"start": v(132.07, -71.3) * mm, "end": v(136.9, -70) * mm});
            skSolve(sketch);
        }
        {
            var Q0;
            Q0=makeQuery(id+"F5.imprint","IMPRINT",FACE,{"disambiguationData":[TD([[makeQuery(id+"F5.imprint","IMPRINT",EDGE,{"derivedFrom":sQuery(id+"F5.wireOp",EDGE,"E7")}),-1.0]])]});
            var Q1;
            Q1=makeQuery(id+"F5.imprint","IMPRINT",FACE,{"disambiguationData":[TD([[makeQuery(id+"F5.imprint","IMPRINT",EDGE,{"derivedFrom":sQuery(id+"F5.wireOp",EDGE,"E9.0")}),-1.0]])]});
            var Q2;
            Q2=makeQuery(id+"F5.imprint","IMPRINT",FACE,{"disambiguationData":[TD([[makeQuery(id+"F5.imprint","IMPRINT",EDGE,{"derivedFrom":sQuery(id+"F5.wireOp",EDGE,"E15.1.0.1")}),1.0]])]});
            var Q3;
            Q3=makeQuery(id+"F5.imprint","IMPRINT",FACE,{"disambiguationData":[TD([[makeQuery(id+"F5.imprint","IMPRINT",EDGE,{"derivedFrom":sQuery(id+"F5.wireOp",EDGE,"E15.1.0.1")}),-1.0]])]});
            var Q4;
            Q4=makeQuery(id+"F5.imprint","IMPRINT",FACE,{"disambiguationData":[TD([[makeQuery(id+"F5.imprint","IMPRINT",EDGE,{"derivedFrom":sQuery(id+"F5.wireOp",EDGE,"E15.2.0.1")}),1.0]])]});
            var Q5;
            Q5=makeQuery(id+"F5.imprint","IMPRINT",FACE,{"disambiguationData":[TD([[makeQuery(id+"F5.imprint","IMPRINT",EDGE,{"derivedFrom":sQuery(id+"F5.wireOp",EDGE,"E15.2.0.1")}),-1.0]])]});
            var Q6;
            Q6=makeQuery(id+"F5.imprint","IMPRINT",FACE,{"disambiguationData":[TD([[makeQuery(id+"F5.imprint","IMPRINT",EDGE,{"derivedFrom":sQuery(id+"F5.wireOp",EDGE,"E16.3.3.0")}),1.0]])]});
            var Q7;
            Q7=makeQuery(id+"F5.imprint","IMPRINT",FACE,{"disambiguationData":[TD([[makeQuery(id+"F5.imprint","IMPRINT",EDGE,{"derivedFrom":sQuery(id+"F5.wireOp",EDGE,"E16.3.3.0")}),-1.0]])]});
            var Q8;
            Q8=makeQuery(id+"F5.imprint","IMPRINT",FACE,{"disambiguationData":[TD([[makeQuery(id+"F5.imprint","IMPRINT",EDGE,{"derivedFrom":sQuery(id+"F5.wireOp",EDGE,"E16.3.4.0")}),1.0]])]});
            var Q9;
            Q9=makeQuery(id+"F5.imprint","IMPRINT",FACE,{"disambiguationData":[TD([[makeQuery(id+"F5.imprint","IMPRINT",EDGE,{"derivedFrom":sQuery(id+"F5.wireOp",EDGE,"E16.3.4.0")}),-1.0]])]});
            var Q10;
            Q10=makeQuery(id+"F5.imprint","IMPRINT",FACE,{"disambiguationData":[TD([[makeQuery(id+"F5.imprint","IMPRINT",EDGE,{"derivedFrom":sQuery(id+"F5.wireOp",EDGE,"E16.3.5.0")}),1.0]])]});
            var Q11;
            Q11=makeQuery(id+"F5.imprint","IMPRINT",FACE,{"disambiguationData":[TD([[makeQuery(id+"F5.imprint","IMPRINT",EDGE,{"derivedFrom":sQuery(id+"F5.wireOp",EDGE,"E16.3.5.0")}),-1.0]])]});
            var Q12;
            Q12=makeQuery(id+"F5.imprint","IMPRINT",FACE,{"disambiguationData":[TD([[makeQuery(id+"F5.imprint","IMPRINT",EDGE,{"derivedFrom":sQuery(id+"F5.wireOp",EDGE,"E16.3.6.0")}),1.0]])]});
            var Q13;
            Q13=makeQuery(id+"F5.imprint","IMPRINT",FACE,{"disambiguationData":[TD([[makeQuery(id+"F5.imprint","IMPRINT",EDGE,{"derivedFrom":sQuery(id+"F5.wireOp",EDGE,"E16.3.6.0")}),-1.0]])]});
            var Q14;
            Q14=makeQuery(id+"F5.imprint","IMPRINT",FACE,{"disambiguationData":[TD([[makeQuery(id+"F5.imprint","IMPRINT",EDGE,{"derivedFrom":sQuery(id+"F5.wireOp",EDGE,"E16.3.7.0")}),1.0]])]});
            var Q15;
            Q15=makeQuery(id+"F5.imprint","IMPRINT",FACE,{"disambiguationData":[TD([[makeQuery(id+"F5.imprint","IMPRINT",EDGE,{"derivedFrom":sQuery(id+"F5.wireOp",EDGE,"E16.3.7.0")}),-1.0]])]});
            var Q16;
            Q16=makeQuery(id+"F5.imprint","IMPRINT",FACE,{"disambiguationData":[TD([[makeQuery(id+"F5.imprint","IMPRINT",EDGE,{"derivedFrom":sQuery(id+"F5.wireOp",EDGE,"E16.3.8.0")}),1.0]])]});
            var Q17;
            Q17=makeQuery(id+"F5.imprint","IMPRINT",FACE,{"disambiguationData":[TD([[makeQuery(id+"F5.imprint","IMPRINT",EDGE,{"derivedFrom":sQuery(id+"F5.wireOp",EDGE,"E16.3.8.0")}),-1.0]])]});
            var Q18;
            Q18=makeQuery(id+"F5.imprint","IMPRINT",FACE,{"disambiguationData":[TD([[makeQuery(id+"F5.imprint","IMPRINT",EDGE,{"derivedFrom":sQuery(id+"F5.wireOp",EDGE,"E16.3.9.0")}),1.0]])]});
            var Q19;
            Q19=makeQuery(id+"F5.imprint","IMPRINT",FACE,{"disambiguationData":[TD([[makeQuery(id+"F5.imprint","IMPRINT",EDGE,{"derivedFrom":sQuery(id+"F5.wireOp",EDGE,"E16.3.9.0")}),-1.0]])]});
            var Q20;
            Q20=makeQuery(id+"F5.imprint","IMPRINT",FACE,{"disambiguationData":[TD([[makeQuery(id+"F5.imprint","IMPRINT",EDGE,{"derivedFrom":sQuery(id+"F5.wireOp",EDGE,"E16.3.10.0")}),1.0]])]});
            var Q21;
            Q21=makeQuery(id+"F5.imprint","IMPRINT",FACE,{"disambiguationData":[TD([[makeQuery(id+"F5.imprint","IMPRINT",EDGE,{"derivedFrom":sQuery(id+"F5.wireOp",EDGE,"E16.3.10.0")}),-1.0]])]});
            var Q22;
            Q22=makeQuery(id+"F5.imprint","IMPRINT",FACE,{"disambiguationData":[TD([[makeQuery(id+"F5.imprint","IMPRINT",EDGE,{"derivedFrom":sQuery(id+"F5.wireOp",EDGE,"E16.3.11.0")}),1.0]])]});
            var Q23;
            Q23=makeQuery(id+"F5.imprint","IMPRINT",FACE,{"disambiguationData":[TD([[makeQuery(id+"F5.imprint","IMPRINT",EDGE,{"derivedFrom":sQuery(id+"F5.wireOp",EDGE,"E16.3.11.0")}),-1.0]])]});
            var Q24;
            Q24=makeQuery(id+"F5.imprint","IMPRINT",FACE,{"disambiguationData":[TD([[makeQuery(id+"F5.imprint","IMPRINT",EDGE,{"derivedFrom":sQuery(id+"F5.wireOp",EDGE,"E16.3.12.0")}),1.0]])]});
            var Q25;
            Q25=makeQuery(id+"F5.imprint","IMPRINT",FACE,{"disambiguationData":[TD([[makeQuery(id+"F5.imprint","IMPRINT",EDGE,{"derivedFrom":sQuery(id+"F5.wireOp",EDGE,"E16.3.12.0")}),-1.0]])]});
            var Q26;
            Q26=makeQuery(id+"F5.imprint","IMPRINT",FACE,{"disambiguationData":[TD([[makeQuery(id+"F5.imprint","IMPRINT",EDGE,{"derivedFrom":sQuery(id+"F5.wireOp",EDGE,"E16.3.13.0")}),1.0]])]});
            var Q27;
            Q27=makeQuery(id+"F5.imprint","IMPRINT",FACE,{"disambiguationData":[TD([[makeQuery(id+"F5.imprint","IMPRINT",EDGE,{"derivedFrom":sQuery(id+"F5.wireOp",EDGE,"E16.3.13.0")}),-1.0]])]});
            var Q28;
            Q28=makeQuery(id+"F5.imprint","IMPRINT",FACE,{"disambiguationData":[TD([[makeQuery(id+"F5.imprint","IMPRINT",EDGE,{"derivedFrom":sQuery(id+"F5.wireOp",EDGE,"E16.3.14.0")}),1.0]])]});
            var Q29;
            Q29=makeQuery(id+"F5.imprint","IMPRINT",FACE,{"disambiguationData":[TD([[makeQuery(id+"F5.imprint","IMPRINT",EDGE,{"derivedFrom":sQuery(id+"F5.wireOp",EDGE,"E16.3.14.0")}),-1.0]])]});
            var Q30;
            Q30=makeQuery(id+"F5.imprint","IMPRINT",FACE,{"disambiguationData":[TD([[makeQuery(id+"F5.imprint","IMPRINT",EDGE,{"derivedFrom":sQuery(id+"F5.wireOp",EDGE,"E16.3.15.0")}),1.0]])]});
            var Q31;
            Q31=makeQuery(id+"F5.imprint","IMPRINT",FACE,{"disambiguationData":[TD([[makeQuery(id+"F5.imprint","IMPRINT",EDGE,{"derivedFrom":sQuery(id+"F5.wireOp",EDGE,"E16.3.15.0")}),-1.0]])]});
            var Q32;
            Q32=makeQuery(id+"F5.imprint","IMPRINT",FACE,{"disambiguationData":[TD([[makeQuery(id+"F5.imprint","IMPRINT",EDGE,{"derivedFrom":sQuery(id+"F5.wireOp",EDGE,"E16.3.16.0")}),1.0]])]});
            var Q33;
            Q33=makeQuery(id+"F5.imprint","IMPRINT",FACE,{"disambiguationData":[TD([[makeQuery(id+"F5.imprint","IMPRINT",EDGE,{"derivedFrom":sQuery(id+"F5.wireOp",EDGE,"E16.3.16.0")}),-1.0]])]});
            var Q34;
            Q34=makeQuery(id+"F5.imprint","IMPRINT",FACE,{"disambiguationData":[TD([[makeQuery(id+"F5.imprint","IMPRINT",EDGE,{"derivedFrom":sQuery(id+"F5.wireOp",EDGE,"E16.3.17.0")}),1.0]])]});
            var Q35;
            Q35=makeQuery(id+"F5.imprint","IMPRINT",FACE,{"disambiguationData":[TD([[makeQuery(id+"F5.imprint","IMPRINT",EDGE,{"derivedFrom":sQuery(id+"F5.wireOp",EDGE,"E16.3.17.0")}),-1.0]])]});
            var Q36;
            Q36=makeQuery(id+"F5.imprint","IMPRINT",FACE,{"disambiguationData":[TD([[makeQuery(id+"F5.imprint","IMPRINT",EDGE,{"derivedFrom":sQuery(id+"F5.wireOp",EDGE,"E16.3.18.0")}),1.0]])]});
            var Q37;
            Q37=makeQuery(id+"F5.imprint","IMPRINT",FACE,{"disambiguationData":[TD([[makeQuery(id+"F5.imprint","IMPRINT",EDGE,{"derivedFrom":sQuery(id+"F5.wireOp",EDGE,"E16.3.18.0")}),-1.0]])]});
            var Q38;
            Q38=makeQuery(id+"F5.imprint","IMPRINT",FACE,{"disambiguationData":[TD([[makeQuery(id+"F5.imprint","IMPRINT",EDGE,{"derivedFrom":sQuery(id+"F5.wireOp",EDGE,"E16.3.19.0")}),1.0]])]});
            var Q39;
            Q39=makeQuery(id+"F5.imprint","IMPRINT",FACE,{"disambiguationData":[TD([[makeQuery(id+"F5.imprint","IMPRINT",EDGE,{"derivedFrom":sQuery(id+"F5.wireOp",EDGE,"E16.3.19.0")}),-1.0]])]});
            var Q40;
            Q40=makeQuery(id+"F5.imprint","IMPRINT",FACE,{"disambiguationData":[TD([[makeQuery(id+"F5.imprint","IMPRINT",EDGE,{"derivedFrom":sQuery(id+"F5.wireOp",EDGE,"E16.3.20.0")}),1.0]])]});
            var Q41;
            Q41=makeQuery(id+"F5.imprint","IMPRINT",FACE,{"disambiguationData":[TD([[makeQuery(id+"F5.imprint","IMPRINT",EDGE,{"derivedFrom":sQuery(id+"F5.wireOp",EDGE,"E16.3.20.0")}),-1.0]])]});
            var Q42;
            Q42=makeQuery(id+"F5.imprint","IMPRINT",FACE,{"disambiguationData":[TD([[makeQuery(id+"F5.imprint","IMPRINT",EDGE,{"derivedFrom":sQuery(id+"F5.wireOp",EDGE,"E16.3.21.0")}),1.0]])]});
            var Q43;
            Q43=makeQuery(id+"F5.imprint","IMPRINT",FACE,{"disambiguationData":[TD([[makeQuery(id+"F5.imprint","IMPRINT",EDGE,{"derivedFrom":sQuery(id+"F5.wireOp",EDGE,"E16.3.21.0")}),-1.0]])]});
            var Q44;
            Q44=makeQuery(id+"F5.imprint","IMPRINT",FACE,{"disambiguationData":[TD([[makeQuery(id+"F5.imprint","IMPRINT",EDGE,{"derivedFrom":sQuery(id+"F5.wireOp",EDGE,"E16.3.22.0")}),1.0]])]});
            var Q45;
            Q45=makeQuery(id+"F5.imprint","IMPRINT",FACE,{"disambiguationData":[TD([[makeQuery(id+"F5.imprint","IMPRINT",EDGE,{"derivedFrom":sQuery(id+"F5.wireOp",EDGE,"E16.3.22.0")}),-1.0]])]});
            var Q46;
            Q46=makeQuery(id+"F5.imprint","IMPRINT",FACE,{"disambiguationData":[TD([[makeQuery(id+"F5.imprint","IMPRINT",EDGE,{"derivedFrom":sQuery(id+"F5.wireOp",EDGE,"E17.3.23.0")}),1.0]])]});
            var Q47;
            Q47=makeQuery(id+"F5.imprint","IMPRINT",FACE,{"disambiguationData":[TD([[makeQuery(id+"F5.imprint","IMPRINT",EDGE,{"derivedFrom":sQuery(id+"F5.wireOp",EDGE,"E17.3.23.0")}),-1.0]])]});
            var Q48;
            Q48=makeQuery(id+"F5.imprint","IMPRINT",FACE,{"disambiguationData":[TD([[makeQuery(id+"F5.imprint","IMPRINT",EDGE,{"derivedFrom":sQuery(id+"F5.wireOp",EDGE,"E17.3.24.0")}),1.0]])]});
            var Q49;
            Q49=makeQuery(id+"F5.imprint","IMPRINT",FACE,{"disambiguationData":[TD([[makeQuery(id+"F5.imprint","IMPRINT",EDGE,{"derivedFrom":sQuery(id+"F5.wireOp",EDGE,"E17.3.24.0")}),-1.0]])]});
            var Q50;
            Q50=makeQuery(id+"F5.imprint","IMPRINT",FACE,{"disambiguationData":[TD([[makeQuery(id+"F5.imprint","IMPRINT",EDGE,{"derivedFrom":sQuery(id+"F5.wireOp",EDGE,"E18.3.25.0")}),1.0]])]});
            var Q51;
            Q51=makeQuery(id+"F5.imprint","IMPRINT",FACE,{"disambiguationData":[TD([[makeQuery(id+"F5.imprint","IMPRINT",EDGE,{"derivedFrom":sQuery(id+"F5.wireOp",EDGE,"E18.3.25.0")}),-1.0]])]});
            var Q52;
            Q52=makeQuery(id+"F5.imprint","IMPRINT",FACE,{"disambiguationData":[TD([[makeQuery(id+"F5.imprint","IMPRINT",EDGE,{"derivedFrom":sQuery(id+"F5.wireOp",EDGE,"E18.3.26.0")}),1.0]])]});
            var Q53;
            Q53=makeQuery(id+"F5.imprint","IMPRINT",FACE,{"disambiguationData":[TD([[makeQuery(id+"F5.imprint","IMPRINT",EDGE,{"derivedFrom":sQuery(id+"F5.wireOp",EDGE,"E18.3.26.0")}),-1.0]])]});
            var Q54;
            Q54=makeQuery(id+"F5.imprint","IMPRINT",FACE,{"disambiguationData":[TD([[makeQuery(id+"F5.imprint","IMPRINT",EDGE,{"derivedFrom":sQuery(id+"F5.wireOp",EDGE,"E18.3.27.0")}),1.0]])]});
            var Q55;
            Q55=makeQuery(id+"F5.imprint","IMPRINT",FACE,{"disambiguationData":[TD([[makeQuery(id+"F5.imprint","IMPRINT",EDGE,{"derivedFrom":sQuery(id+"F5.wireOp",EDGE,"E18.3.27.0")}),-1.0]])]});
            var Q56;
            Q56=makeQuery(id+"F5.imprint","IMPRINT",FACE,{"disambiguationData":[TD([[makeQuery(id+"F5.imprint","IMPRINT",EDGE,{"derivedFrom":sQuery(id+"F5.wireOp",EDGE,"7cc6724f-c960-404d-9fb9-fa70a4dc17af.0")}),1.0]])]});
            var Q57;
            Q57=makeQuery(id+"F5.imprint","IMPRINT",FACE,{"disambiguationData":[TD([[makeQuery(id+"F5.imprint","IMPRINT",EDGE,{"derivedFrom":sQuery(id+"F5.wireOp",EDGE,"E19.3.28.0")}),1.0]])]});
            var Q58;
            Q58=makeQuery(id+"F5.imprint","IMPRINT",FACE,{"disambiguationData":[TD([[makeQuery(id+"F5.imprint","IMPRINT",EDGE,{"derivedFrom":sQuery(id+"F5.wireOp",EDGE,"E19.3.28.0")}),-1.0]])]});
            var Q59;
            Q59=makeQuery(id+"F5.imprint","IMPRINT",FACE,{"disambiguationData":[TD([[makeQuery(id+"F5.imprint","IMPRINT",EDGE,{"derivedFrom":sQuery(id+"F5.wireOp",EDGE,"E19.3.29.0")}),1.0]])]});
            var Q60;
            Q60=makeQuery(id+"F5.imprint","IMPRINT",FACE,{"disambiguationData":[TD([[makeQuery(id+"F5.imprint","IMPRINT",EDGE,{"derivedFrom":sQuery(id+"F5.wireOp",EDGE,"E19.3.29.0")}),-1.0]])]});
            var Q61;
            Q61=makeQuery(id+"F5.imprint","IMPRINT",FACE,{"disambiguationData":[TD([[makeQuery(id+"F5.imprint","IMPRINT",EDGE,{"derivedFrom":sQuery(id+"F5.wireOp",EDGE,"E22.0")}),1.0]])]});
            extrude(context, id + "F6", {"entities" : qUnion([Q0, Q1, Q2, Q3, Q4, Q5, Q6, Q7, Q8, Q9, Q10, Q11, Q12, Q13, Q14, Q15, Q16, Q17, Q18, Q19, Q20, Q21, Q22, Q23, Q24, Q25, Q26, Q27, Q28, Q29, Q30, Q31, Q32, Q33, Q34, Q35, Q36, Q37, Q38, Q39, Q40, Q41, Q42, Q43, Q44, Q45, Q46, Q47, Q48, Q49, Q50, Q51, Q52, Q53, Q54, Q55, Q56, Q57, Q58, Q59, Q60, Q61]), "operationType" : NewBodyOperationType.REMOVE, "oppositeDirection" : true, "depth" : 15 * mm});
        }
    });
